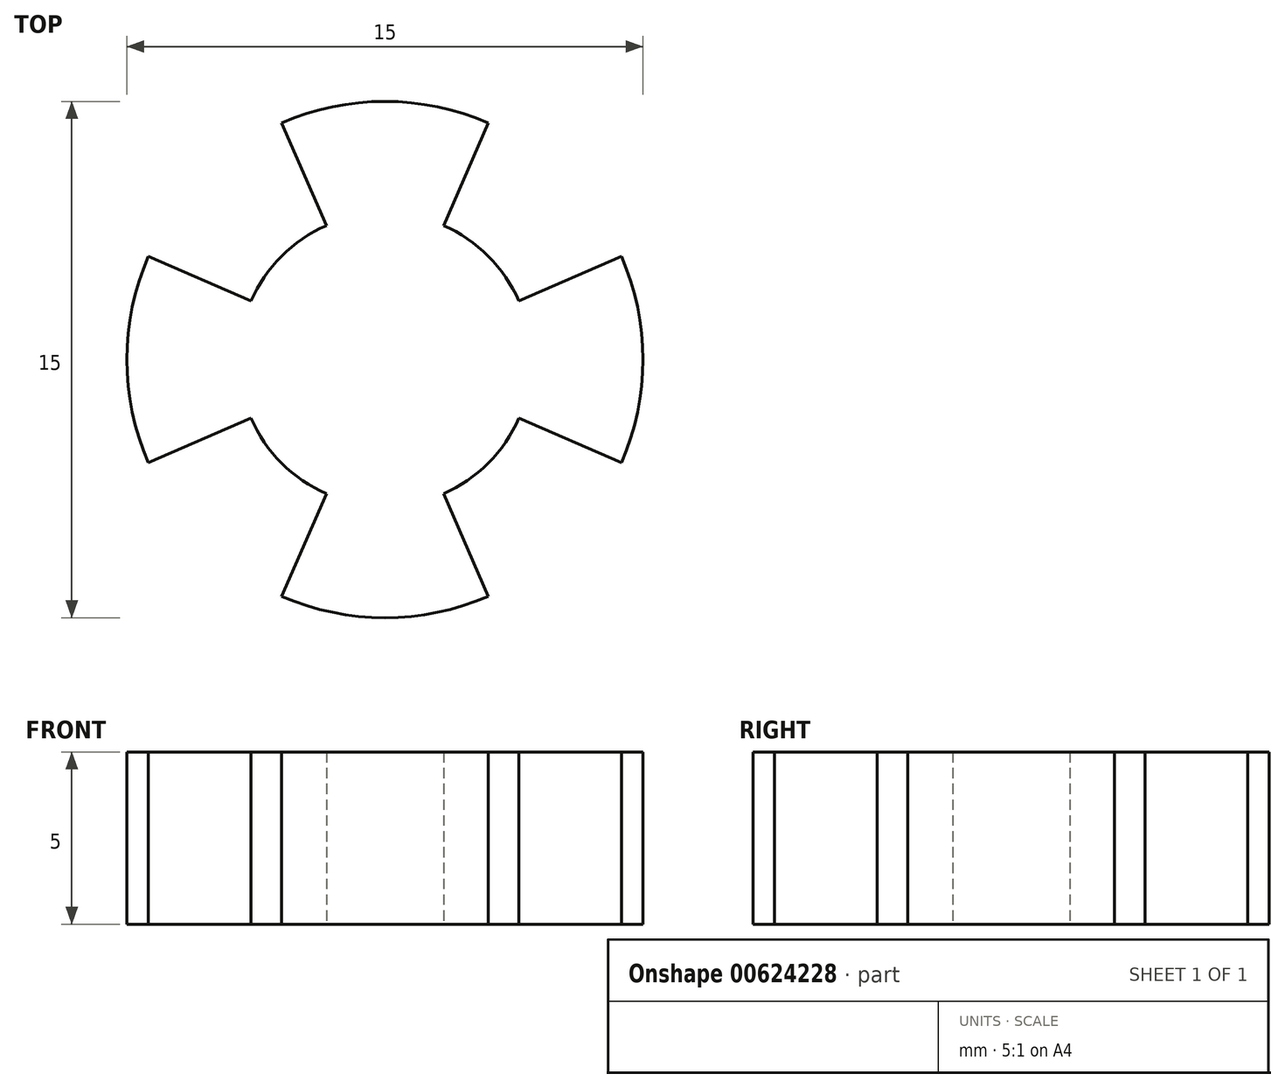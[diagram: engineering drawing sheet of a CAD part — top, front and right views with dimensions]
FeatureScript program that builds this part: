
annotation { "Feature Type Name" : "Feature", "Feature Type Description" : "" }
export const myFeature = defineFeature(function(context is Context, id is Id, definition is map)
    precondition{}
    {
        {
            var Q0;
            Q0=qCreatedBy(makeId("Top.planeOp"),FACE);
            var sketch = newSketch(context, id + "F0", { "sketchPlane" : qUnion([Q0])});
            skCircle(sketch, "E0", {"center": v(0, 0) * mm, "radius": 7.5 * mm});
            skCircle(sketch, "E1", {"center": v(0, 0) * mm, "radius": 4.25 * mm});
            skLineSegment(sketch, "E2", {"start": v(1.7, 3.9) * mm, "end": v(3, 6.87) * mm});
            skLineSegment(sketch, "E3.MirrorCS", {"start": v(-1.7, 3.9) * mm, "end": v(-3, 6.87) * mm});
            skLineSegment(sketch, "E4.1.0", {"start": v(-3.9, 1.7) * mm, "end": v(-6.87, 3) * mm});
            skLineSegment(sketch, "E4.1.1", {"start": v(-3.9, -1.7) * mm, "end": v(-6.87, -3) * mm});
            skLineSegment(sketch, "E4.2.0", {"start": v(-1.7, -3.9) * mm, "end": v(-3, -6.87) * mm});
            skLineSegment(sketch, "E4.2.1", {"start": v(1.7, -3.9) * mm, "end": v(3, -6.87) * mm});
            skLineSegment(sketch, "E4.3.0", {"start": v(3.9, -1.7) * mm, "end": v(6.87, -3) * mm});
            skLineSegment(sketch, "E4.3.1", {"start": v(3.9, 1.7) * mm, "end": v(6.87, 3) * mm});
            skSolve(sketch);
        }
        {
            var Q0;
            {var subQ0=sQuery(id+"F0.wireOp",EDGE,"E2");Q0=makeQuery(id+"F0.imprint","IMPRINT",FACE,{"disambiguationData":[TD([[makeQuery(id+"F0.imprint","IMPRINT",EDGE,{"derivedFrom":subQ0}),1.0]])]});}
            var Q1;
            {var subQ0=sQuery(id+"F0.wireOp",EDGE,"E4.3.0");Q1=makeQuery(id+"F0.imprint","IMPRINT",FACE,{"disambiguationData":[TD([[makeQuery(id+"F0.imprint","IMPRINT",EDGE,{"derivedFrom":subQ0}),1.0]])]});}
            var Q2;
            {var subQ0=sQuery(id+"F0.wireOp",EDGE,"E4.2.0");Q2=makeQuery(id+"F0.imprint","IMPRINT",FACE,{"disambiguationData":[TD([[makeQuery(id+"F0.imprint","IMPRINT",EDGE,{"derivedFrom":subQ0}),1.0]])]});}
            var Q3;
            {var subQ0=sQuery(id+"F0.wireOp",EDGE,"E4.1.0");Q3=makeQuery(id+"F0.imprint","IMPRINT",FACE,{"disambiguationData":[TD([[makeQuery(id+"F0.imprint","IMPRINT",EDGE,{"derivedFrom":subQ0}),1.0]])]});}
            var Q4;
            {var subQ0=sQuery(id+"F0.wireOp",EDGE,"E1");var subQ4=makeQuery(id+"F0.imprint","INTERSECT",VERTEX,{"derivedFrom":[subQ0,sQuery(id+"F0.wireOp",EDGE,"E2")]});Q4=makeQuery(id+"F0.imprint","IMPRINT",FACE,{"disambiguationData":[TD([[makeQuery(id+"F0.imprint","IMPRINT",EDGE,{"disambiguationData":[TD([[subQ4,1.0]])],"derivedFrom":subQ0}),1.0]])]});}
            extrude(context, id + "F1", {"entities" : qUnion([Q0, Q1, Q2, Q3, Q4]), "depth" : 5 * mm, "offsetDistance" : 25 * mm});
        }
    });
